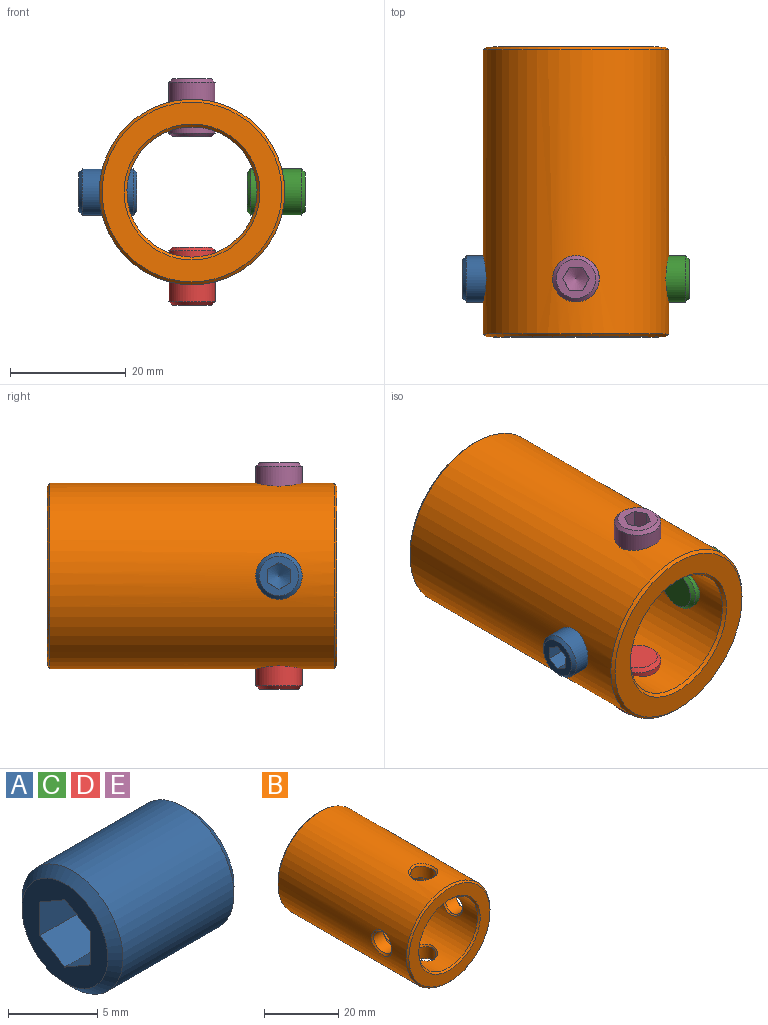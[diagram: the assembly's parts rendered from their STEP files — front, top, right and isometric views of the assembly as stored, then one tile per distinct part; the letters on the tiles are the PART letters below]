
ASSEMBLY  parts=5 mates=1
PART A: 12 faces, bbox 10x8x8 mm
  f0: plane 6.8x6.8mm, normal (-1,0,0), area 22.5mm2, adj f4,f5,f6,f7,f8,f9,f10
  f1: plane 6.8x6.8mm, normal (1,0,0), area 36.3mm2, adj f2
  f2: cone r=3.4mm half-angle=45deg, axis (-1,0,0), area 19.7mm2, adj f1,f3
  f3: cylinder r=4mm len=8.8mm, axis (-1,0,0), area 221.2mm2, adj f2,f4
  f4: cone r=4mm half-angle=45deg, axis (1,0,0), area 19.7mm2, adj f0,f3
  f5: plane 3.18x2mm, normal (0,-0.5,-0.87), area 7.2mm2, adj f0,f6,f10,f11
  f6: plane 3.18x2mm, normal (0,0.5,-0.87), area 7.2mm2, adj f0,f5,f7,f11
  f7: plane 3.18x2.31mm, normal (0,1,0), area 7.2mm2, adj f0,f6,f8,f11
  f8: plane 3.18x2mm, normal (0,0.5,0.87), area 7.2mm2, adj f0,f7,f9,f11
  f9: plane 3.18x2mm, normal (0,-0.5,0.87), area 7.2mm2, adj f0,f8,f10,f11
  f10: plane 3.18x2.31mm, normal (0,-1,0), area 7.2mm2, adj f0,f5,f9,f11
  f11: cone r=0mm half-angle=60deg, axis (-1,0,0), area 16mm2, adj f5,f6,f7,f8,f9,f10
PART B: 20 faces, bbox 32x50x32 mm
  f0: cylinder r=16mm len=49mm, axis (0,-1,0), area 4736.8mm2, adj f14,f15,f16,f17,f18,f19
  f1: cylinder r=11.23mm len=49mm, axis (0,-1,0), area 3271mm2, adj f8,f9,f10,f11,f12,f13
  f2: plane 31x31mm, normal (0,1,0), area 322.9mm2, adj f12,f18
  f3: plane 31x31mm, normal (0,-1,0), area 322.9mm2, adj f13,f19
  f4: cylinder r=3.4mm len=6.8mm, axis (0,0,1), area 84.2mm2, adj f10,f16
  f5: cylinder r=3.4mm len=6.8mm, axis (0,0,1), area 77.1mm2, adj f11,f17
  f6: cylinder r=3.4mm len=6.8mm, axis (-1,0,0), area 84.2mm2, adj f9,f15
  f7: cylinder r=3.4mm len=6.8mm, axis (-1,0,0), area 84.2mm2, adj f8,f14
  f8: bspline ~7.8x7.47mm, area 14.7mm2, adj f1,f7
  f9: bspline ~7.8x7.47mm, area 14.7mm2, adj f1,f6
  f10: bspline ~7.8x7.47mm, area 14.7mm2, adj f1,f4
  f11: bspline ~7.8x7.47mm, area 14.7mm2, adj f1,f5
  f12: cone r=11.73mm half-angle=45deg, axis (0,1,0), area 51mm2, adj f1,f2
  f13: cone r=11.23mm half-angle=45deg, axis (0,-1,0), area 51mm2, adj f1,f3
  f14: bspline ~8.05x7.8mm, area 17.4mm2, adj f0,f7
  f15: bspline ~8.05x7.8mm, area 17.4mm2, adj f0,f6
  f16: bspline ~8.05x7.8mm, area 17.4mm2, adj f0,f4
  f17: bspline ~8.04x7.8mm, area 17.4mm2, adj f0,f5
  f18: cone r=16mm half-angle=45deg, axis (0,-1,0), area 70mm2, adj f0,f2
  f19: cone r=15.5mm half-angle=45deg, axis (0,1,0), area 70mm2, adj f0,f3
PART C: same geometry as A
PART D: same geometry as A
PART E: same geometry as A
PLACE A rot(axis=(1,0,0),180deg) t=(-64.83,51.89,-3.22)mm
PLACE B t=(0,-0.5,0)mm
PLACE C rot(axis=(0,0,1),180deg) t=(64.83,51.89,3.22)mm
PLACE D rot(axis=(0.71,0,0.71),180deg) t=(3.22,51.89,-64.83)mm
PLACE E rot(axis=(0.71,0,-0.71),180deg) t=(-3.22,51.89,64.83)mm
MATE fastened B.f4 <-> E.f2  axis (0,0,1) through (0,9.5,15.53)mm
